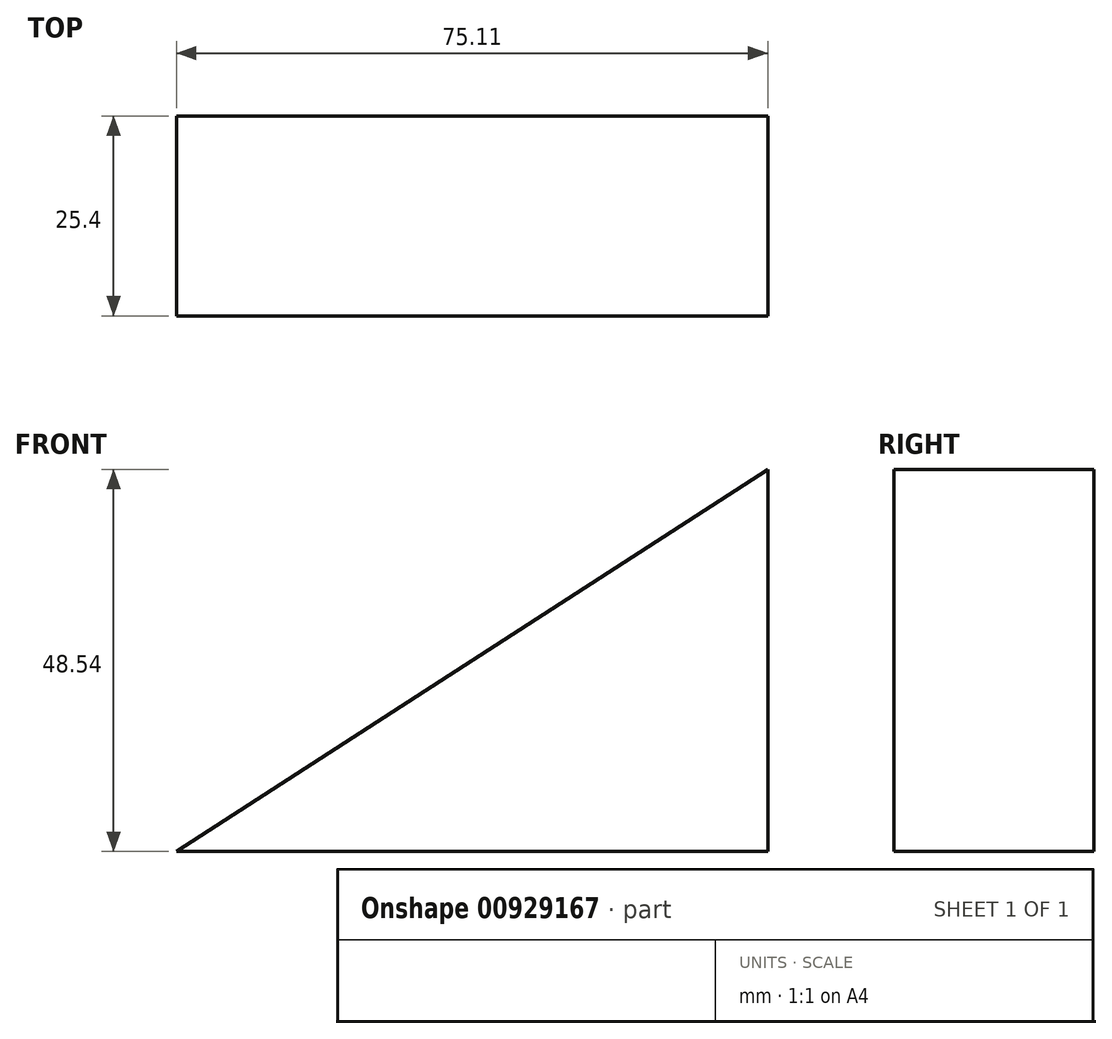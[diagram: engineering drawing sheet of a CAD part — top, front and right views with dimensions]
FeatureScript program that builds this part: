
annotation { "Feature Type Name" : "Feature", "Feature Type Description" : "" }
export const myFeature = defineFeature(function(context is Context, id is Id, definition is map)
    precondition{}
    {
        {
            var Q0;
            Q0=qCreatedBy(makeId("Front.planeOp"),FACE);
            var sketch = newSketch(context, id + "F0", { "sketchPlane" : qUnion([Q0])});
            skLineSegment(sketch, "E0", {"start": v(0, 0) * mm, "end": v(0, 48.54) * mm});
            skLineSegment(sketch, "E1", {"start": v(0, 48.54) * mm, "end": v(-75.11, 0) * mm});
            skLineSegment(sketch, "E2", {"start": v(-75.11, 0) * mm, "end": v(0, 0) * mm});
            skSolve(sketch);
        }
        {
            var Q0;
            Q0=makeQuery(id+"F0.imprint","IMPRINT",FACE,{"disambiguationData":[TD([[makeQuery(id+"F0.imprint","IMPRINT",EDGE,{"derivedFrom":sQuery(id+"F0.wireOp",EDGE,"E0")}),1.0]])]});
            extrude(context, id + "F1", {"entities" : qUnion([Q0]), "depth" : 25.4 * mm, "offsetDistance" : 25.4 * mm});
        }
    });
